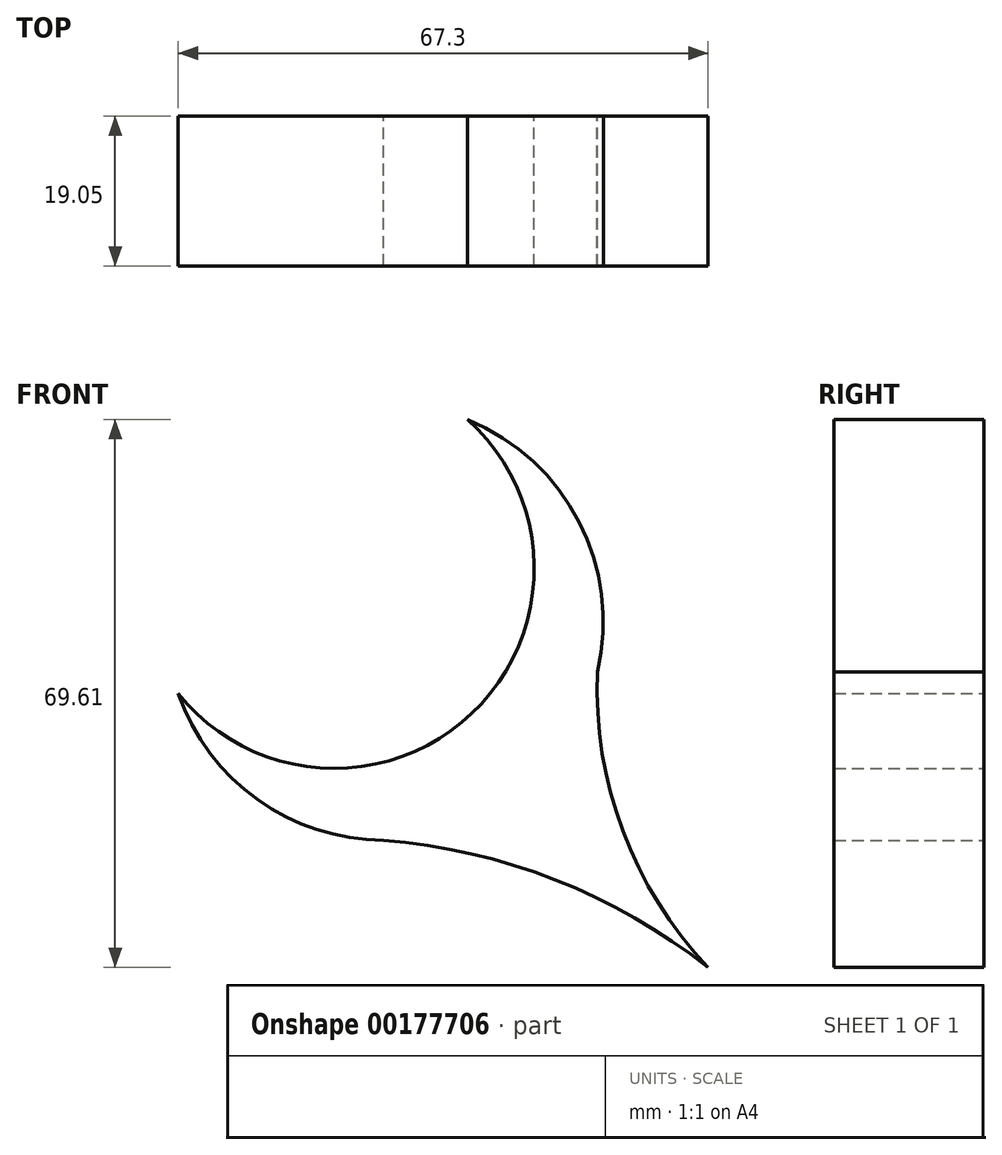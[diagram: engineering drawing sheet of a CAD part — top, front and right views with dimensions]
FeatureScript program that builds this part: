
annotation { "Feature Type Name" : "Feature", "Feature Type Description" : "" }
export const myFeature = defineFeature(function(context is Context, id is Id, definition is map)
    precondition{}
    {
        {
            var Q0;
            Q0=qCreatedBy(makeId("Front.planeOp"),FACE);
            var sketch = newSketch(context, id + "F0", { "sketchPlane" : qUnion([Q0])});
            skArc(sketch, "E0", {"start": v(0, 6.14) * mm, "mid": v(37.28, 3.6) * mm, "end": v(36.75, 40.96) * mm});
            skArc(sketch, "E1", {"start": v(0, 6.14) * mm, "mid": v(45.32, -4.9) * mm, "end": v(36.75, 40.96) * mm});
            skArc(sketch, "E2", {"start": v(53.99, 15.73) * mm, "mid": v(55.37, -8.04) * mm, "end": v(67.3, -28.65) * mm});
            skArc(sketch, "E3", {"start": v(67.3, -28.65) * mm, "mid": v(46.51, -16.98) * mm, "end": v(23.14, -12.33) * mm});
            skPoint(sketch, "E4", {"position": v(37.28, 3.6) * mm});
            skSolve(sketch);
        }
        {
            var Q0;
            Q0 = qSketchRegion(id + "F0", true);
            extrude(context, id + "F1", {"entities" : qUnion([Q0]), "depth" : 19.05 * mm});
        }
    });
